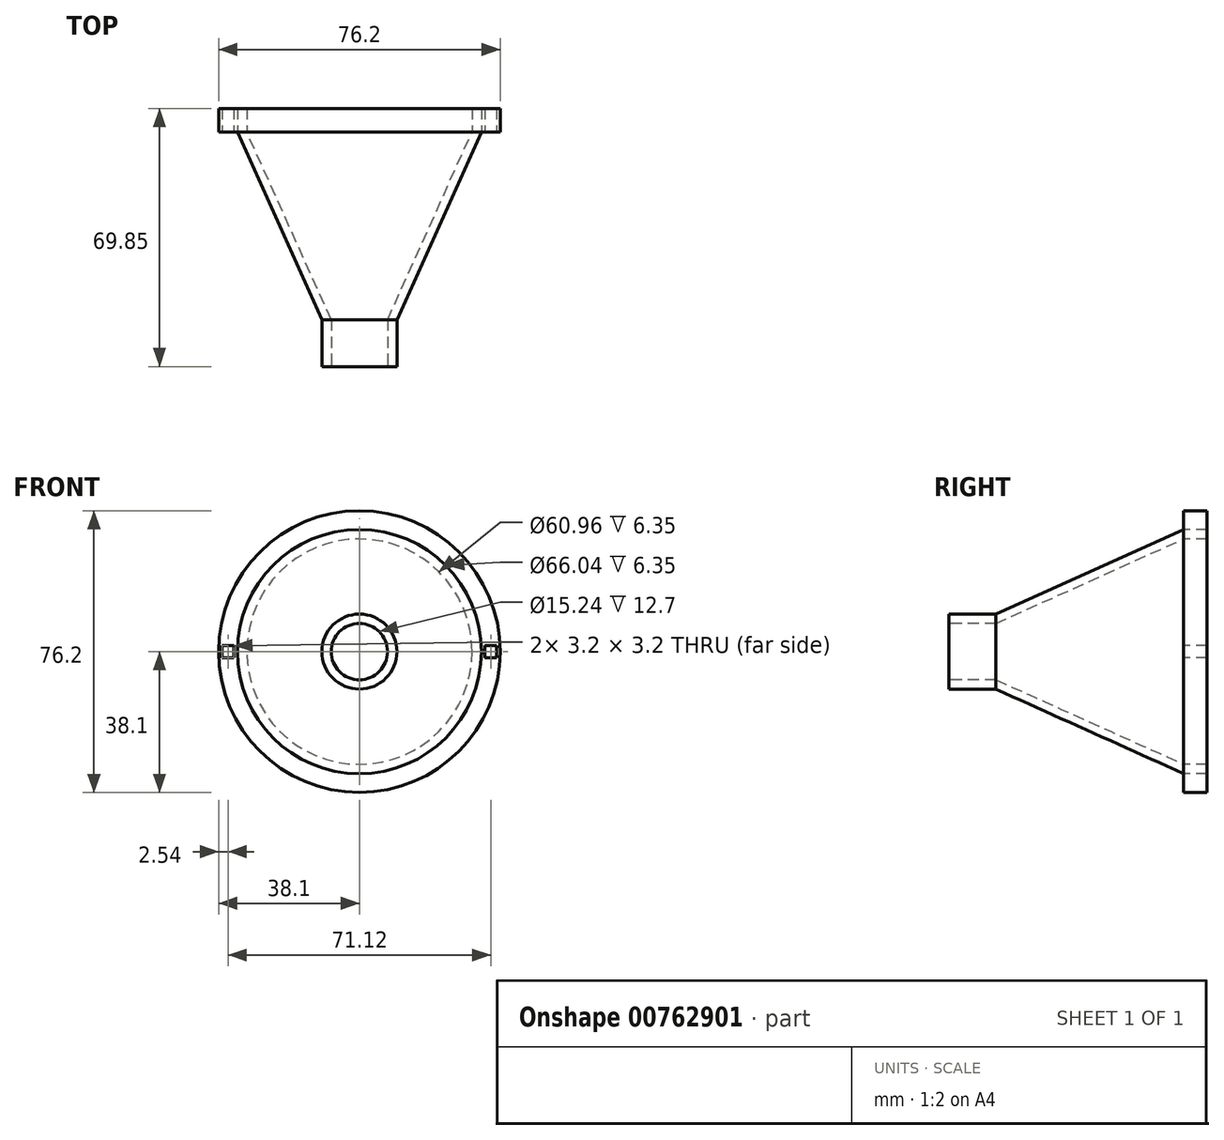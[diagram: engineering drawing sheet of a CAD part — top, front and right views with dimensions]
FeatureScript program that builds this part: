
annotation { "Feature Type Name" : "Feature", "Feature Type Description" : "" }
export const myFeature = defineFeature(function(context is Context, id is Id, definition is map)
    precondition{}
    {
        {
            var Q0;
            Q0=qCreatedBy(makeId("Top.planeOp"),FACE);
            var sketch = newSketch(context, id + "F0", { "sketchPlane" : qUnion([Q0])});
            skLineSegment(sketch, "E0", {"start": v(0, 0) * mm, "end": v(0, 12.7) * mm});
            skLineSegment(sketch, "E1", {"start": v(0, 12.7) * mm, "end": v(-2.54, 12.7) * mm});
            skLineSegment(sketch, "E2", {"start": v(-2.54, 12.7) * mm, "end": v(-2.54, 0) * mm});
            skLineSegment(sketch, "E3", {"start": v(-2.54, 0) * mm, "end": v(0, 0) * mm});
            skLineSegment(sketch, "E4", {"start": v(0, 63.5) * mm, "end": v(-25.4, 63.5) * mm});
            skLineSegment(sketch, "E5", {"start": v(-22.86, 63.5) * mm, "end": v(-25.4, 63.5) * mm});
            skLineSegment(sketch, "E6", {"start": v(0, 63.5) * mm, "end": v(0, 12.7) * mm});
            skLineSegment(sketch, "E7", {"start": v(-25.4, 63.5) * mm, "end": v(-2.54, 12.7) * mm});
            skLineSegment(sketch, "E8", {"start": v(-22.86, 63.5) * mm, "end": v(0, 12.7) * mm});
            skLineSegment(sketch, "E9", {"start": v(0, 0) * mm, "end": v(7.62, 0) * mm});
            skLineSegment(sketch, "E10", {"start": v(7.62, 0) * mm, "end": v(7.62, 69.83) * mm});
            skSolve(sketch);
        }
        {
            var Q0;
            Q0=makeQuery(id+"F0.imprint","IMPRINT",FACE,{"disambiguationData":[TD([[makeQuery(id+"F0.imprint","IMPRINT",EDGE,{"derivedFrom":sQuery(id+"F0.wireOp",EDGE,"E1")}),-1.0]])]});
            var Q1;
            Q1=makeQuery(id+"F0.imprint","IMPRINT",FACE,{"disambiguationData":[TD([[makeQuery(id+"F0.imprint","IMPRINT",EDGE,{"derivedFrom":sQuery(id+"F0.wireOp",EDGE,"E0")}),1.0]])]});
            var Q2;
            Q2=sQuery(id+"F0.wireOp",EDGE,"E10");
            revolve(context, id + "F1", {"surfaceOperationType" : NewSurfaceOperationType.NEW, "entities" : qUnion([Q0, Q1]), "axis" : qUnion([Q2]), "revolveType" : RevolveType.FULL});
        }
        {
            var Q0;
            Q0=makeQuery(id+"F1.opRevolve","SWEPT_FACE",FACE,{"disambiguationData":[OSD([sQuery(id+"F0.wireOp",EDGE,"E4")])]});
            var sketch = newSketch(context, id + "F2", { "sketchPlane" : qUnion([Q0])});
            skCircle(sketch, "E11", {"center": v(-7.62, 0) * mm, "radius": 38.1 * mm});
            skCircle(sketch, "E12.0", {"center": v(-7.62, 0) * mm, "radius": 33.02 * mm});
            skCircle(sketch, "E13.0", {"center": v(-7.62, 0) * mm, "radius": 30.48 * mm});
            skLineSegment(sketch, "E14", {"start": v(-43.18, -1.6) * mm, "end": v(-41.58, -1.6) * mm});
            skLineSegment(sketch, "E15", {"start": v(-43.18, 1.6) * mm, "end": v(-44.78, 1.6) * mm});
            skLineSegment(sketch, "E16.bottom", {"start": v(-41.58, -1.6) * mm, "end": v(-44.78, -1.6) * mm});
            skLineSegment(sketch, "E16.top", {"start": v(-41.58, 1.6) * mm, "end": v(-44.78, 1.6) * mm});
            skLineSegment(sketch, "E16.left", {"start": v(-41.58, -1.6) * mm, "end": v(-41.58, 1.6) * mm});
            skLineSegment(sketch, "E16.right", {"start": v(-44.78, -1.6) * mm, "end": v(-44.78, 1.6) * mm});
            skLineSegment(sketch, "E17", {"start": v(-7.62, 0) * mm, "end": v(-7.62, -21.9) * mm});
            skLineSegment(sketch, "E18.MirrorCS", {"start": v(26.34, -1.6) * mm, "end": v(26.34, 1.6) * mm});
            skLineSegment(sketch, "E19.MirrorCS", {"start": v(26.34, -1.6) * mm, "end": v(29.54, -1.6) * mm});
            skLineSegment(sketch, "E20.MirrorCS", {"start": v(29.54, -1.6) * mm, "end": v(29.54, 1.6) * mm});
            skLineSegment(sketch, "E21.MirrorCS", {"start": v(26.34, 1.6) * mm, "end": v(29.54, 1.6) * mm});
            skLineSegment(sketch, "E22.MirrorCS", {"start": v(27.94, -1.6) * mm, "end": v(26.34, -1.6) * mm});
            skLineSegment(sketch, "E23.MirrorCS", {"start": v(27.94, 1.6) * mm, "end": v(29.54, 1.6) * mm});
            skSolve(sketch);
        }
        {
            var Q0;
            Q0 = qSketchRegion(id + "F2", true);
            extrude(context, id + "F3", {"entities" : qUnion([Q0]), "depth" : 6.35 * mm, "offsetDistance" : 25.4 * mm});
        }
        {
            var Q0;
            Q0=makeQuery(id+"F1.opRevolve","SWEPT_FACE",FACE,{"disambiguationData":[OSD([sQuery(id+"F0.wireOp",EDGE,"E4")])]});
            var sketch = newSketch(context, id + "F4", { "sketchPlane" : qUnion([Q0])});
            skCircle(sketch, "E24.0", {"center": v(-7.62, 0) * mm, "radius": 30.48 * mm});
            skCircle(sketch, "E25.0", {"center": v(-7.62, 0) * mm, "radius": 33.02 * mm});
            skSolve(sketch);
        }
        {
            var Q0;
            Q0=makeQuery(id+"F4.imprint","IMPRINT",FACE,{"disambiguationData":[TD([[makeQuery(id+"F4.imprint","IMPRINT",EDGE,{"derivedFrom":sQuery(id+"F4.wireOp",EDGE,"E24.0")}),1.0]])]});
            extrude(context, id + "F5", {"entities" : qUnion([Q0]), "depth" : 6.35 * mm, "offsetDistance" : 25.4 * mm});
        }
    });
